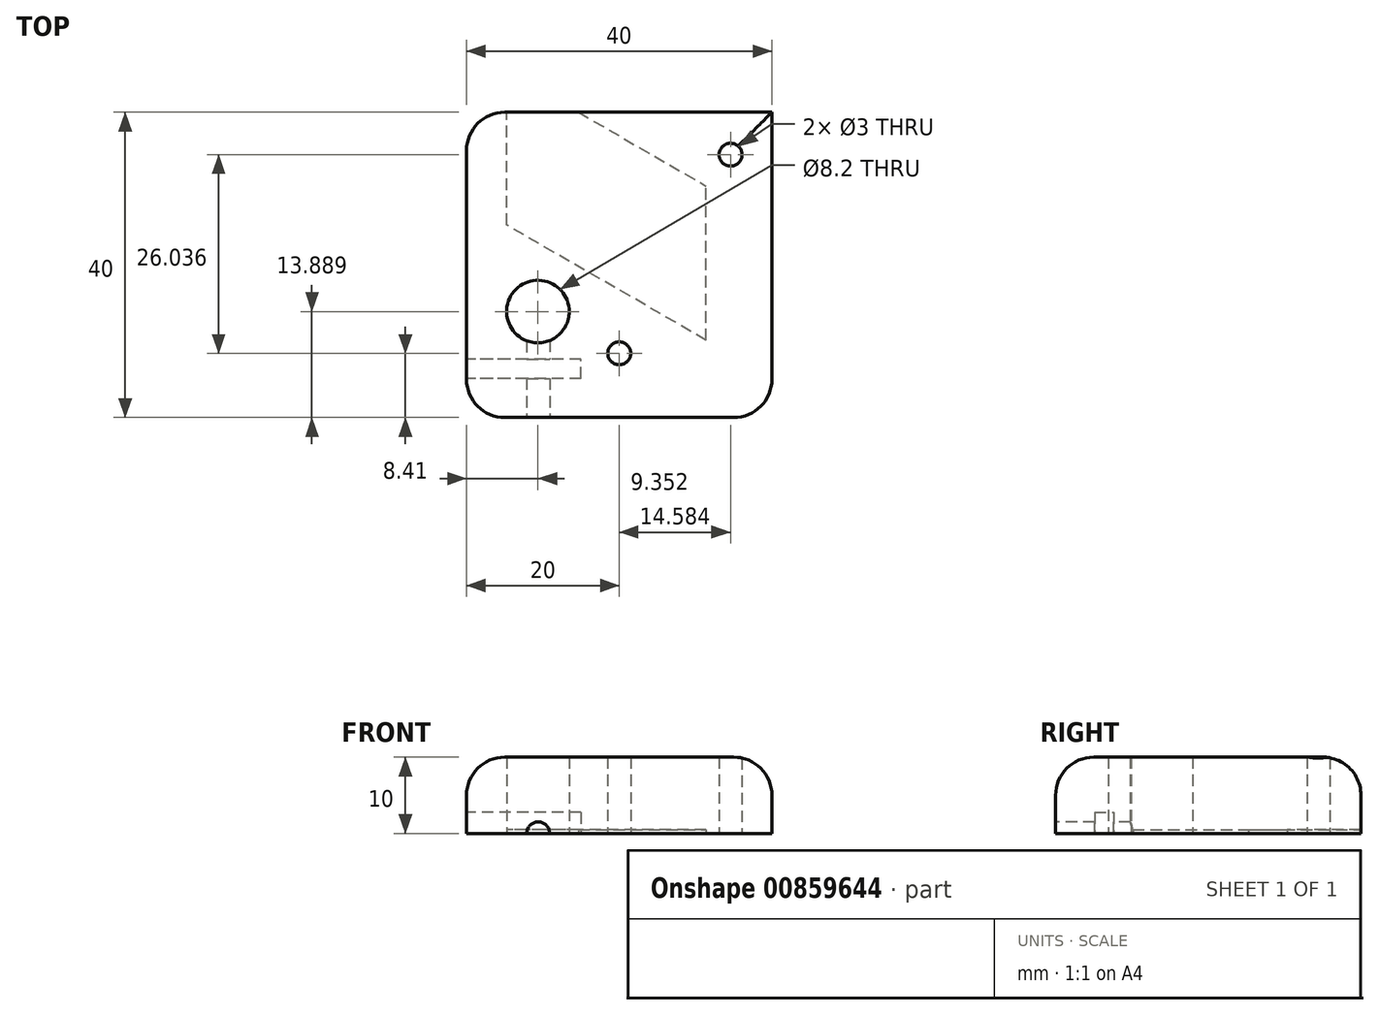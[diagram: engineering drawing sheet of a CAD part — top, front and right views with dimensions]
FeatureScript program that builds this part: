
annotation { "Feature Type Name" : "Feature", "Feature Type Description" : "" }
export const myFeature = defineFeature(function(context is Context, id is Id, definition is map)
    precondition{}
    {
        {
            var Q0;
            Q0=qCreatedBy(makeId("Top.planeOp"),FACE);
            var sketch = newSketch(context, id + "F0", { "sketchPlane" : qUnion([Q0])});
            skLineSegment(sketch, "E0.bottom", {"start": v(20, -20) * mm, "end": v(-20, -20) * mm});
            skLineSegment(sketch, "E0.top", {"start": v(20, 20) * mm, "end": v(-20, 20) * mm});
            skLineSegment(sketch, "E0.left", {"start": v(20, -20) * mm, "end": v(20, 20) * mm});
            skLineSegment(sketch, "E0.right", {"start": v(-20, -20) * mm, "end": v(-20, 20) * mm});
            skPoint(sketch, "E0.middle", {"position": v(0, 0) * mm});
            skSolve(sketch);
        }
        {
            var Q0;
            Q0=makeQuery(id+"F0.imprint","IMPRINT",FACE,{"disambiguationData":[TD([[makeQuery(id+"F0.imprint","IMPRINT",EDGE,{"derivedFrom":sQuery(id+"F0.wireOp",EDGE,"E0.bottom")}),-1.0]])]});
            extrude(context, id + "F1", {"entities" : qUnion([Q0]), "depth" : 10 * mm, "offsetDistance" : 25 * mm});
        }
        {
            var Q0;
            Q0=makeQuery(id+"F1.opExtrude","CAP_FACE",FACE,{"disambiguationData":[OSD([sQuery(id+"F0.wireOp",EDGE,"E0.bottom"),sQuery(id+"F0.wireOp",EDGE,"E0.top"),sQuery(id+"F0.wireOp",EDGE,"E0.left"),sQuery(id+"F0.wireOp",EDGE,"E0.right")])],"isStart":true});
            var sketch = newSketch(context, id + "F2", { "sketchPlane" : qUnion([Q0])});
            skLineSegment(sketch, "E1", {"start": v(-14.76, -5.23) * mm, "end": v(-14.76, -25.43) * mm});
            skLineSegment(sketch, "E2", {"start": v(-14.76, -25.43) * mm, "end": v(11.4, -10.33) * mm});
            skLineSegment(sketch, "E3", {"start": v(11.4, 9.87) * mm, "end": v(-14.76, -5.23) * mm});
            skLineSegment(sketch, "E4", {"start": v(11.4, 9.87) * mm, "end": v(11.4, -10.33) * mm});
            skSolve(sketch);
        }
        {
            var Q0;
            {var subQ0=sQuery(id+"F2.wireOp",EDGE,"E3");Q0=makeQuery(id+"F2.imprint","IMPRINT",FACE,{"disambiguationData":[TD([[makeQuery(id+"F2.imprint","IMPRINT",EDGE,{"derivedFrom":subQ0}),1.0]])]});}
            extrude(context, id + "F3", {"entities" : qUnion([Q0]), "operationType" : NewBodyOperationType.REMOVE, "oppositeDirection" : true, "depth" : 0.5 * mm, "offsetDistance" : 25 * mm});
        }
        {
            var Q0;
            Q0=makeQuery(id+"F1.opExtrude","CAP_FACE",FACE,{"disambiguationData":[OSD([sQuery(id+"F0.wireOp",EDGE,"E0.bottom"),sQuery(id+"F0.wireOp",EDGE,"E0.top"),sQuery(id+"F0.wireOp",EDGE,"E0.left"),sQuery(id+"F0.wireOp",EDGE,"E0.right")])],"isStart":true});
            var sketch = newSketch(context, id + "F4", { "sketchPlane" : qUnion([Q0])});
            skCircle(sketch, "E5", {"center": v(-10.65, 6.11) * mm, "radius": 4.1 * mm});
            skSolve(sketch);
        }
        {
            var Q0;
            Q0=makeQuery(id+"F4.imprint","IMPRINT",FACE,{"disambiguationData":[TD([[makeQuery(id+"F4.imprint","IMPRINT",EDGE,{"derivedFrom":sQuery(id+"F4.wireOp",EDGE,"E5")}),1.0]])]});
            extrude(context, id + "F5", {"entities" : qUnion([Q0]), "operationType" : NewBodyOperationType.REMOVE, "endBound" : BoundingType.THROUGH_ALL, "oppositeDirection" : true, "depth" : 25 * mm, "offsetDistance" : 25 * mm});
        }
        {
            var Q0;
            Q0=makeQuery(id+"F1.opExtrude","CAP_FACE",FACE,{"disambiguationData":[OSD([sQuery(id+"F0.wireOp",EDGE,"E0.bottom"),sQuery(id+"F0.wireOp",EDGE,"E0.top"),sQuery(id+"F0.wireOp",EDGE,"E0.left"),sQuery(id+"F0.wireOp",EDGE,"E0.right")])],"isStart":true});
            var sketch = newSketch(context, id + "F6", { "sketchPlane" : qUnion([Q0])});
            skLineSegment(sketch, "E6", {"start": v(-14.75, 6.2) * mm, "end": v(-20, 6.2) * mm, "construction": true});
            skSolve(sketch);
        }
        {
            var Q0;
            Q0=makeQuery(id+"F1.opExtrude","SWEPT_FACE",FACE,{"disambiguationData":[OSD([sQuery(id+"F0.wireOp",EDGE,"E0.right")])]});
            var sketch = newSketch(context, id + "F7", { "sketchPlane" : qUnion([Q0])});
            skLineSegment(sketch, "E7.bottom", {"start": v(14.88, 2.75) * mm, "end": v(12.38, 2.75) * mm});
            skLineSegment(sketch, "E7.top", {"start": v(14.88, -2.75) * mm, "end": v(12.38, -2.75) * mm});
            skLineSegment(sketch, "E7.left", {"start": v(14.88, 2.75) * mm, "end": v(14.88, -2.75) * mm});
            skLineSegment(sketch, "E7.right", {"start": v(12.38, 2.75) * mm, "end": v(12.38, -2.75) * mm});
            skPoint(sketch, "E7.middle", {"position": v(13.63, 0) * mm});
            skSolve(sketch);
        }
        {
            var Q0;
            {var subQ0=sQuery(id+"F7.wireOp",EDGE,"E7.bottom");Q0=makeQuery(id+"F7.imprint","IMPRINT",FACE,{"disambiguationData":[TD([[makeQuery(id+"F7.imprint","IMPRINT",EDGE,{"derivedFrom":subQ0}),1.0]])]});}
            extrude(context, id + "F8", {"entities" : qUnion([Q0]), "operationType" : NewBodyOperationType.REMOVE, "oppositeDirection" : true, "depth" : 15 * mm, "offsetDistance" : 25 * mm});
        }
        {
            var Q0;
            {var subQ3=sQuery(id+"F0.wireOp",EDGE,"E0.bottom");Q0=makeQuery(id+"F6.imprint","IMPRINT",FACE,{"disambiguationData":[TD([[makeQuery(id+"F6.imprint","IMPRINT",EDGE,{"derivedFrom":makeQuery(id+"F1.opExtrude","CAP_EDGE",EDGE,{"disambiguationData":[OSD([subQ3])],"isStart":true})}),1.0]])]});}
            var sketch = newSketch(context, id + "F9", { "sketchPlane" : qUnion([Q0])});
            skLineSegment(sketch, "E8", {"start": v(-10.61, 10.23) * mm, "end": v(-10.61, 20) * mm, "construction": true});
            skSolve(sketch);
        }
        {
            var Q0;
            Q0=makeQuery(id+"F1.opExtrude","SWEPT_FACE",FACE,{"disambiguationData":[OSD([sQuery(id+"F0.wireOp",EDGE,"E0.bottom")])]});
            var sketch = newSketch(context, id + "F10", { "sketchPlane" : qUnion([Q0])});
            skCircle(sketch, "E9", {"center": v(-10.61, 0) * mm, "radius": 1.5 * mm});
            skSolve(sketch);
        }
        {
            var Q0;
            {var subQ0=sQuery(id+"F10.wireOp",EDGE,"E9");var subQ1=makeQuery(id+"F1.opExtrude","CAP_EDGE",EDGE,{"disambiguationData":[OSD([sQuery(id+"F0.wireOp",EDGE,"E0.bottom")])],"isStart":true});var subQ2=makeQuery(id+"F10.imprint","INTERSECT",VERTEX,{"disambiguationData":[OD(0.0)],"derivedFrom":[subQ1,subQ0]});Q0=makeQuery(id+"F10.imprint","IMPRINT",FACE,{"disambiguationData":[TD([[makeQuery(id+"F10.imprint","IMPRINT",EDGE,{"disambiguationData":[TD([[subQ2,-1.0]])],"derivedFrom":subQ0}),1.0]])]});}
            var Q1;
            Q1=makeQuery(id+"F5.boolean.opBoolean","COPY",FACE,{"derivedFrom":makeQuery(id+"F5.opExtrude","SWEPT_FACE",FACE,{"disambiguationData":[OSD([sQuery(id+"F4.wireOp",EDGE,"E5")])]})});
            var Q2;
            Q2=sQuery(id+"F9.wireOp",VERTEX,"E8.start");
            extrude(context, id + "F11", {"entities" : qUnion([Q0]), "operationType" : NewBodyOperationType.REMOVE, "endBound" : BoundingType.UP_TO_SURFACE, "oppositeDirection" : true, "depth" : 25 * mm, "endBoundEntityFace" : qUnion([Q1]), "endBoundEntityVertex" : qUnion([Q2]), "offsetDistance" : 25 * mm});
        }
        {
            var Q0;
            {var subQ3=sQuery(id+"F0.wireOp",EDGE,"E0.bottom");Q0=makeQuery(id+"F6.imprint","IMPRINT",FACE,{"disambiguationData":[TD([[makeQuery(id+"F6.imprint","IMPRINT",EDGE,{"derivedFrom":makeQuery(id+"F1.opExtrude","CAP_EDGE",EDGE,{"disambiguationData":[OSD([subQ3])],"isStart":true})}),1.0]])]});}
            var sketch = newSketch(context, id + "F12", { "sketchPlane" : qUnion([Q0])});
            skCircle(sketch, "E10", {"center": v(0, 11.6) * mm, "radius": 1.5 * mm});
            skCircle(sketch, "E11", {"center": v(14.58, -14.45) * mm, "radius": 1.5 * mm});
            skSolve(sketch);
        }
        {
            var Q0;
            Q0 = qSketchRegion(id + "F12", true);
            extrude(context, id + "F13", {"entities" : qUnion([Q0]), "operationType" : NewBodyOperationType.REMOVE, "endBound" : BoundingType.THROUGH_ALL, "oppositeDirection" : true, "depth" : 25 * mm, "offsetDistance" : 25 * mm});
        }
        {
            var Q0;
            Q0=makeQuery(id+"F1.opExtrude","SWEPT_EDGE",EDGE,{"disambiguationData":[OSD([sQuery(id+"F0.wireOp",EDGE,"E0.bottom"),sQuery(id+"F0.wireOp",EDGE,"E0.right")])]});
            var Q1;
            Q1=makeQuery(id+"F1.opExtrude","SWEPT_EDGE",EDGE,{"disambiguationData":[OSD([sQuery(id+"F0.wireOp",EDGE,"E0.top"),sQuery(id+"F0.wireOp",EDGE,"E0.right")])]});
            var Q2;
            Q2=makeQuery(id+"F1.opExtrude","SWEPT_EDGE",EDGE,{"disambiguationData":[OSD([sQuery(id+"F0.wireOp",EDGE,"E0.bottom"),sQuery(id+"F0.wireOp",EDGE,"E0.left")])]});
            var Q3;
            Q3=makeQuery(id+"F1.opExtrude","CAP_EDGE",EDGE,{"disambiguationData":[OSD([sQuery(id+"F0.wireOp",EDGE,"E0.left")])],"isStart":false});
            var Q4;
            Q4=makeQuery(id+"F1.opExtrude","CAP_EDGE",EDGE,{"disambiguationData":[OSD([sQuery(id+"F0.wireOp",EDGE,"E0.bottom")])],"isStart":false});
            var Q5;
            Q5=makeQuery(id+"F1.opExtrude","CAP_EDGE",EDGE,{"disambiguationData":[OSD([sQuery(id+"F0.wireOp",EDGE,"E0.right")])],"isStart":false});
            var Q6;
            Q6=makeQuery(id+"F1.opExtrude","CAP_EDGE",EDGE,{"disambiguationData":[OSD([sQuery(id+"F0.wireOp",EDGE,"E0.top")])],"isStart":false});
            fillet(context, id + "F14", {"entities" : qUnion([Q0, Q1, Q2, Q3, Q4, Q5, Q6]), "radius" : 5 * mm, "tangentPropagation" : true, "allowEdgeOverflow" : false});
        }
    });
